# Revit family: B2306
name_source: partatom
category: Apparecchi idraulici
units: mm (PartAtom-declared; Revit-internal decimal feet)

## family parameters
Basato su piano di lavoro = No
Condiviso = No
Mantieni orientamento annotazione = No
Numero OmniClass = 23.45.55.17
Punto di calcolo locali = No
Quota connettore circolare = Usa diametro
Sempre verticale = Sì
Taglio con vuoti quando caricato = No
Tipo di parte = Normale
Titolo OmniClass = Mixing Faucets

## types (13) — shared parameters
Cold water inlet = 10 mm  [stored 0.0328084 ft]
Commenti sul tipo = Wall mounted widespread lavatory faucet
Connessione CW = No
Connessione HW = No
Connessione di scarico = No
Connessione di ventilazione = No
Descrizione = Wall mounted widespread lavatory faucet
Hot water inlet = 10 mm  [stored 0.0328084 ft]
Produttore = IB Rubinetterie S.p.A.
URL = https://www.weareib.it
zero-valued in all types: Prospetto di default

## per-type parameters (varying)
| type | Finishes surface | Immagine tipo | Modello |
| Chrome | IB_Chrome | B2306CC.jpg | B2306CC |
| Black Chrome | IB_Black chrome | B2306CF.jpg | B2306CF |
| Brushed Black Chrome | IB_Brushed black chrome | B2306CS.jpg | B2306CS |
| Pale Gold | IB_Pale gold | B2306II.jpg | B2306II |
| Brushed Pale Gold | IB_brushed pale gold | B2306IS.jpg | B2306IS |
| Matt Black | IB_matt black | B2306NP.jpg | B2306NP |
| Natural Brass | IB_Brass | B2306ON.jpg | B2306ON |
| Gold | IB_gold | B2306OO.jpg | B2306OO |
| Brushed Gold | IB_brushed gold | B2306OS.jpg | B2306OS |
| Rose Gold | IB_Rose gold | B2306RS.jpg | B2306RS |
| Brushed Rose Gold | IB_Brushed rose gold | B2306SR.jpg | B2306SR |
| Brushed Nickel | IB_Brushed nickel | B2306SS.jpg | B2306SS |
| Modern Bronze | IB_Modern bronze | B2306MB.jpg | B2306MB |

note: [stored X ft] marks values corroborated as IEEE doubles in the binary element streams (Revit-internal decimal feet)
